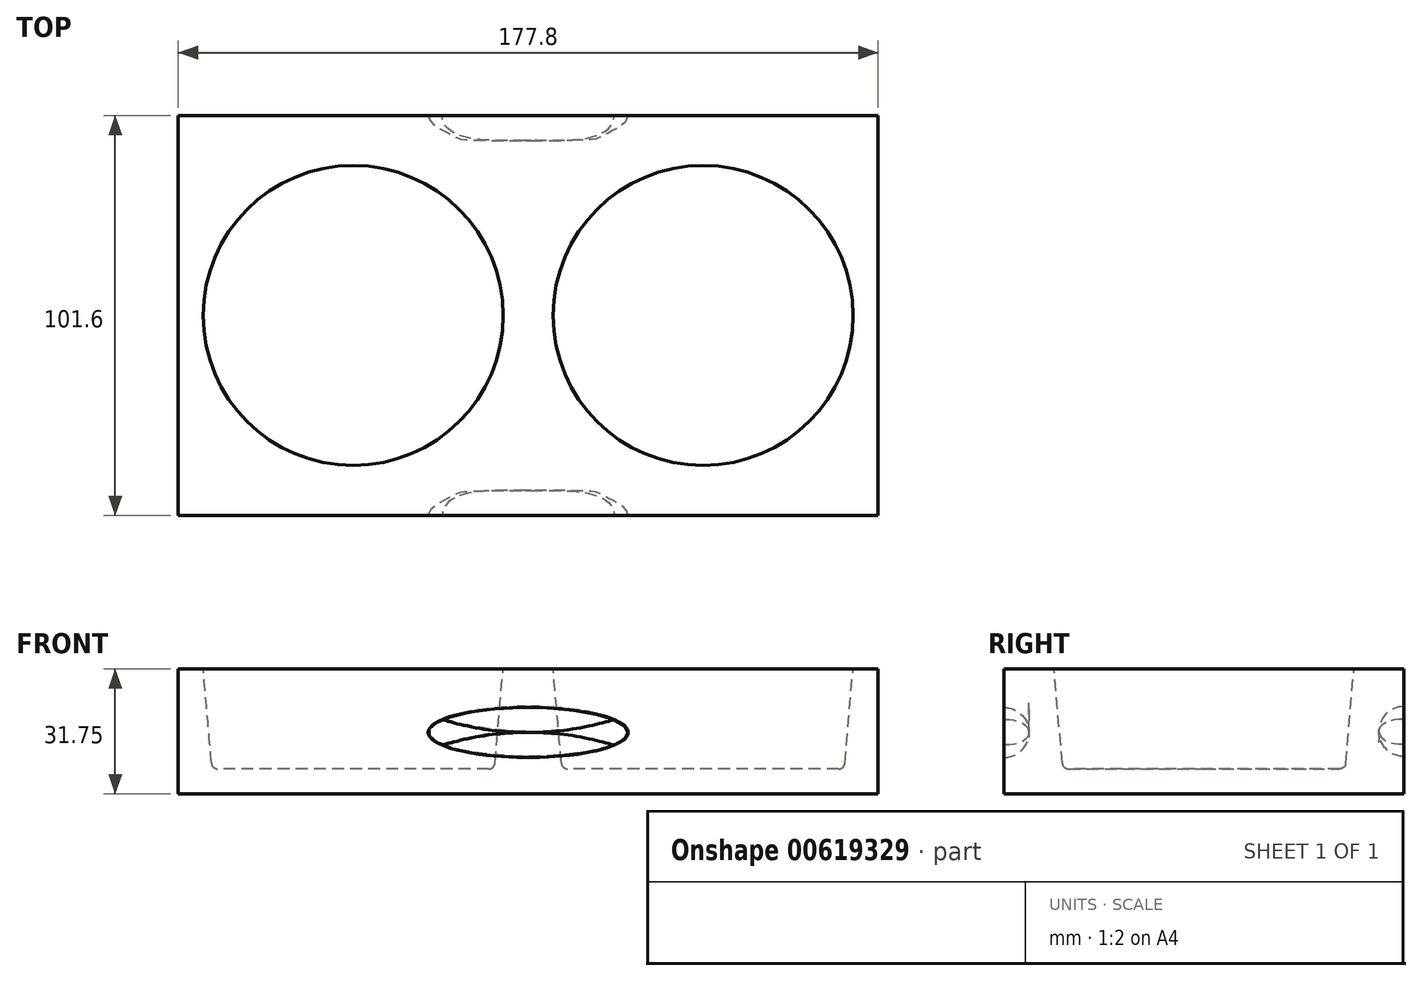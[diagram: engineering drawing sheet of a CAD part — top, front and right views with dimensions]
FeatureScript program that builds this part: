
annotation { "Feature Type Name" : "Feature", "Feature Type Description" : "" }
export const myFeature = defineFeature(function(context is Context, id is Id, definition is map)
    precondition{}
    {
        {
            var Q0;
            Q0=qCreatedBy(makeId("Top.planeOp"),FACE);
            var sketch = newSketch(context, id + "F0", { "sketchPlane" : qUnion([Q0])});
            skLineSegment(sketch, "E0.bottom", {"start": v(88.9, -50.8) * mm, "end": v(-88.9, -50.8) * mm});
            skLineSegment(sketch, "E0.top", {"start": v(88.9, 50.8) * mm, "end": v(-88.9, 50.8) * mm});
            skLineSegment(sketch, "E0.left", {"start": v(88.9, -50.8) * mm, "end": v(88.9, 50.8) * mm});
            skLineSegment(sketch, "E0.right", {"start": v(-88.9, -50.8) * mm, "end": v(-88.9, 50.8) * mm});
            skPoint(sketch, "E0.middle", {"position": v(0, 0) * mm});
            skSolve(sketch);
        }
        {
            var Q0;
            Q0=makeQuery(id+"F0.imprint","IMPRINT",FACE,{"disambiguationData":[TD([[makeQuery(id+"F0.imprint","IMPRINT",EDGE,{"derivedFrom":sQuery(id+"F0.wireOp",EDGE,"E0.bottom")}),-1.0]])]});
            extrude(context, id + "F1", {"entities" : qUnion([Q0]), "depth" : 31.75 * mm, "offsetDistance" : 25.4 * mm});
        }
        {
            var Q0;
            Q0=makeQuery(id+"F1.opExtrude","CAP_FACE",FACE,{"disambiguationData":[OSD([sQuery(id+"F0.wireOp",EDGE,"E0.bottom"),sQuery(id+"F0.wireOp",EDGE,"E0.top"),sQuery(id+"F0.wireOp",EDGE,"E0.left"),sQuery(id+"F0.wireOp",EDGE,"E0.right")])],"isStart":false});
            var sketch = newSketch(context, id + "F2", { "sketchPlane" : qUnion([Q0])});
            skCircle(sketch, "E1", {"center": v(-44.45, 0) * mm, "radius": 38.1 * mm});
            skCircle(sketch, "E2", {"center": v(44.45, 0) * mm, "radius": 38.1 * mm});
            skSolve(sketch);
        }
        {
            var Q0;
            Q0=makeQuery(id+"F2.imprint","IMPRINT",FACE,{"disambiguationData":[TD([[makeQuery(id+"F2.imprint","IMPRINT",EDGE,{"derivedFrom":sQuery(id+"F2.wireOp",EDGE,"E2")}),1.0]])]});
            var Q1;
            Q1=makeQuery(id+"F2.imprint","IMPRINT",FACE,{"disambiguationData":[TD([[makeQuery(id+"F2.imprint","IMPRINT",EDGE,{"derivedFrom":sQuery(id+"F2.wireOp",EDGE,"E1")}),1.0]])]});
            extrude(context, id + "F3", {"entities" : qUnion([Q0, Q1]), "operationType" : NewBodyOperationType.REMOVE, "oppositeDirection" : true, "depth" : 25.4 * mm, "offsetDistance" : 25.4 * mm, "hasDraft" : true, "draftAngle" : 5 * degree, "draftPullDirection" : true});
        }
        {
            var Q0;
            Q0=makeQuery(id+"F3.boolean.opBoolean","COPY",EDGE,{"derivedFrom":makeQuery(id+"F3.opExtrude","CAP_EDGE",EDGE,{"disambiguationData":[OSD([sQuery(id+"F2.wireOp",EDGE,"E1")])],"isStart":false})});
            var Q1;
            Q1=makeQuery(id+"F3.boolean.opBoolean","COPY",EDGE,{"derivedFrom":makeQuery(id+"F3.opExtrude","CAP_EDGE",EDGE,{"disambiguationData":[OSD([sQuery(id+"F2.wireOp",EDGE,"E2")])],"isStart":false})});
            fillet(context, id + "F4", {"entities" : qUnion([Q0, Q1]), "radius" : 1.59 * mm, "tangentPropagation" : true, "allowEdgeOverflow" : false});
        }
        {
            var Q0;
            Q0=makeQuery(id+"F1.opExtrude","SWEPT_FACE",FACE,{"disambiguationData":[OSD([sQuery(id+"F0.wireOp",EDGE,"E0.bottom")])]});
            var sketch = newSketch(context, id + "F5", { "sketchPlane" : qUnion([Q0])});
            skEllipse(sketch, "E3", {"center": v(0, 15.62) * mm, "majorRadius": 25.4 * mm, "minorRadius": 6.35 * mm, "majorAxis": v(1, 0)});
            skSolve(sketch);
        }
        {
            var Q0;
            Q0=makeQuery(id+"F1.opExtrude","SWEPT_FACE",FACE,{"disambiguationData":[OSD([sQuery(id+"F0.wireOp",EDGE,"E0.top")])]});
            var sketch = newSketch(context, id + "F6", { "sketchPlane" : qUnion([Q0])});
            skEllipse(sketch, "E4", {"center": v(0, 15.88) * mm, "majorRadius": 25.4 * mm, "minorRadius": 6.35 * mm, "majorAxis": v(1, 0)});
            skSolve(sketch);
        }
        {
            var Q0;
            Q0 = qSketchRegion(id + "F5", true);
            extrude(context, id + "F7", {"entities" : qUnion([Q0]), "operationType" : NewBodyOperationType.REMOVE, "oppositeDirection" : true, "depth" : 6.35 * mm, "offsetDistance" : 25.4 * mm});
        }
        {
            var Q0;
            Q0 = qSketchRegion(id + "F6", true);
            extrude(context, id + "F8", {"entities" : qUnion([Q0]), "operationType" : NewBodyOperationType.REMOVE, "oppositeDirection" : true, "depth" : 6.35 * mm, "offsetDistance" : 25.4 * mm});
        }
        {
            var Q0;
            Q0=makeQuery(id+"F8.boolean.opBoolean","COPY",EDGE,{"derivedFrom":makeQuery(id+"F8.opExtrude","CAP_EDGE",EDGE,{"disambiguationData":[OSD([sQuery(id+"F6.wireOp",EDGE,"E4")])],"isStart":false})});
            var Q1;
            Q1=makeQuery(id+"F7.boolean.opBoolean","COPY",EDGE,{"derivedFrom":makeQuery(id+"F7.opExtrude","CAP_EDGE",EDGE,{"disambiguationData":[OSD([sQuery(id+"F5.wireOp",EDGE,"E3")])],"isStart":false})});
            fillet(context, id + "F9", {"entities" : qUnion([Q0, Q1]), "radius" : 6.35 * mm, "tangentPropagation" : true, "allowEdgeOverflow" : false});
        }
    });
